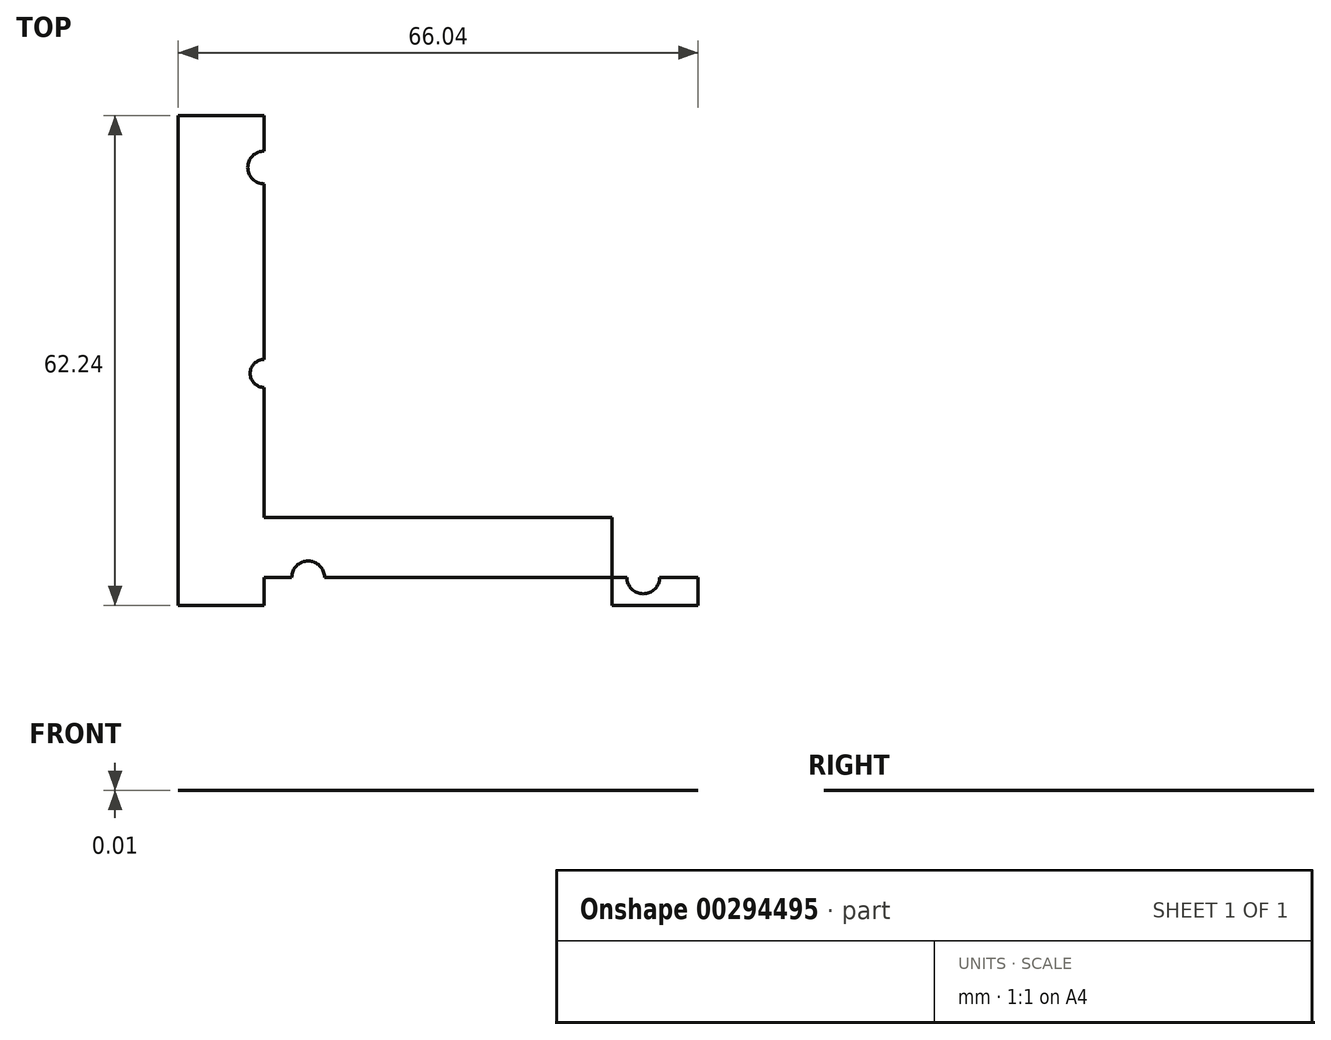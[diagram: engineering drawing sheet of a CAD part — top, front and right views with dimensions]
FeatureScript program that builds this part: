
annotation { "Feature Type Name" : "Feature", "Feature Type Description" : "" }
export const myFeature = defineFeature(function(context is Context, id is Id, definition is map)
    precondition{}
    {
        {
            var Q0;
            Q0=qCreatedBy(makeId("Top.planeOp"),FACE);
            var sketch = newSketch(context, id + "F0", { "sketchPlane" : qUnion([Q0])});
            skLineSegment(sketch, "E0.bottom", {"start": v(33.02, 31.12) * mm, "end": v(-33.02, 31.12) * mm});
            skLineSegment(sketch, "E0.top", {"start": v(33.02, -31.12) * mm, "end": v(-33.02, -31.12) * mm});
            skLineSegment(sketch, "E0.left", {"start": v(33.02, 31.12) * mm, "end": v(33.02, -31.12) * mm});
            skLineSegment(sketch, "E0.right", {"start": v(-33.02, 31.12) * mm, "end": v(-33.02, -31.12) * mm});
            skPoint(sketch, "E0.middle", {"position": v(0, 0) * mm});
            skLineSegment(sketch, "E1.bottom", {"start": v(22.1, 31.12) * mm, "end": v(-22.1, 31.12) * mm});
            skLineSegment(sketch, "E1.top", {"start": v(22.1, -31.12) * mm, "end": v(-22.1, -31.12) * mm});
            skLineSegment(sketch, "E1.left", {"start": v(22.1, 31.11) * mm, "end": v(22.1, -31.12) * mm});
            skLineSegment(sketch, "E1.right", {"start": v(-22.1, 31.11) * mm, "end": v(-22.1, -31.12) * mm});
            skCircle(sketch, "E2", {"center": v(22.1, 24.51) * mm, "radius": 2.08 * mm});
            skCircle(sketch, "E3", {"center": v(22.1, -1.65) * mm, "radius": 2.08 * mm});
            skCircle(sketch, "E4", {"center": v(-22.1, 24.51) * mm, "radius": 2.08 * mm});
            skCircle(sketch, "E5", {"center": v(-22.1, -1.65) * mm, "radius": 1.78 * mm});
            skLineSegment(sketch, "E6.bottom", {"start": v(-22.1, -9.78) * mm, "end": v(22.1, -9.78) * mm});
            skLineSegment(sketch, "E6.top", {"start": v(-22.1, -19.94) * mm, "end": v(22.1, -19.94) * mm});
            skLineSegment(sketch, "E6.left", {"start": v(-22.1, -9.78) * mm, "end": v(-22.1, -19.94) * mm});
            skLineSegment(sketch, "E6.right", {"start": v(22.1, -9.78) * mm, "end": v(22.1, -19.94) * mm});
            skLineSegment(sketch, "E7", {"start": v(-22.1, -27.56) * mm, "end": v(33.02, -27.56) * mm});
            skCircle(sketch, "E8", {"center": v(-16.51, -27.56) * mm, "radius": 2.08 * mm});
            skCircle(sketch, "E9", {"center": v(26.05, -27.56) * mm, "radius": 2.08 * mm});
            skLineSegment(sketch, "E10", {"start": v(0, 0) * mm, "end": v(0, 31.12) * mm});
            skSolve(sketch);
        }
        {
            var Q0;
            {var subQ9=sQuery(id+"F0.wireOp",EDGE,"E1.bottom");Q0=makeQuery(id+"F0.imprint","IMPRINT",FACE,{"disambiguationData":[TD([[makeQuery(id+"F0.imprint","IMPRINT",EDGE,{"derivedFrom":subQ9}),1.0]])]});}
            var Q1;
            {var subQ0=sQuery(id+"F0.wireOp",EDGE,"E0.right");Q1=makeQuery(id+"F0.imprint","IMPRINT",FACE,{"disambiguationData":[TD([[makeQuery(id+"F0.imprint","IMPRINT",EDGE,{"derivedFrom":subQ0}),1.0]])]});}
            var Q2;
            {var subQ6=sQuery(id+"F0.wireOp",EDGE,"E0.left");Q2=makeQuery(id+"F0.imprint","IMPRINT",FACE,{"disambiguationData":[TD([[makeQuery(id+"F0.imprint","IMPRINT",EDGE,{"derivedFrom":subQ6}),-1.0]])]});}
            var Q3;
            {var subQ5=sQuery(id+"F0.wireOp",EDGE,"E6.top");Q3=makeQuery(id+"F0.imprint","IMPRINT",FACE,{"disambiguationData":[TD([[makeQuery(id+"F0.imprint","IMPRINT",EDGE,{"derivedFrom":subQ5}),-1.0]])]});}
            var Q4;
            {var subQ1=sQuery(id+"F0.wireOp",EDGE,"E1.top");Q4=makeQuery(id+"F0.imprint","IMPRINT",FACE,{"disambiguationData":[TD([[makeQuery(id+"F0.imprint","IMPRINT",EDGE,{"derivedFrom":subQ1}),-1.0]])]});}
            var Q5;
            {var subQ5=sQuery(id+"F0.wireOp",EDGE,"E6.right");Q5=makeQuery(id+"F0.imprint","IMPRINT",FACE,{"disambiguationData":[TD([[makeQuery(id+"F0.imprint","IMPRINT",EDGE,{"derivedFrom":subQ5}),1.0]])]});}
            extrude(context, id + "F1", {"entities" : qUnion([Q0, Q1, Q2, Q3, Q4, Q5]), "depth" : 3 / 406.4 * mm});
        }
    });
